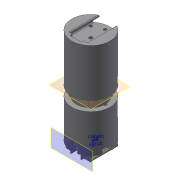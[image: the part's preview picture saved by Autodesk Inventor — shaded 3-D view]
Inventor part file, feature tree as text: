
AUTODESK INVENTOR PART (.ipt)
format: ipt  version: 2018 (Build 220112000, 112)  size: 440,832 bytes
history: native  units: mm
features: sketch x20, extrude x16, fillet x2, plane x2, loft x2, other x2, mirror x1
ambient origin geometry x8: Origin, YZ Plane, XZ Plane, XY Plane, X Axis, Y Axis, Z Axis, Center Point
bodies: Solid1 (feature_tree)
feature tree (45):
  extrude  "base"  Depth=80.0mm TaperAngle=0.0deg
  extrude  "tail_horse_1"  Depth=20.0mm
  mirror  "tail_horse_2"
  fillet  "fillet_tail_horse"  [1 undecoded]
  extrude  "attach_screw"  Depth=20.0mm
  extrude  "attach_screw_head"  Depth=20.0mm TaperAngle=0.0deg
  extrude  "lock_arm"  Depth=30.0mm
  plane  "Work Plane1"
  extrude  "servo_place"  Depth=80.0mm TaperAngle=360.0deg
  sketch  "Sketch7"  dims[d18=0.0mm d19=0.0mm d20=30.0mm]
  sketch  "Sketch8"  dims[d21=6.0mm d22=80.0mm d24=360.0deg]
  sketch  "Sketch9"  dims[d26=20.0mm d27=0.0mm d28=8.0mm]
  extrude  "Extrusion8"  Depth=30.0mm
  extrude  "Extrusion9"  Depth=80.0mm TaperAngle=360.0deg
  sketch  "Sketch12"  dims[d32=10.0mm d33=25.0mm]
  sketch  "Sketch13"  dims[d34=20.0mm d35=65.0mm d36=0.0mm]
  loft  "Loft1"
  loft  "Loft3"
  extrude  "holgura"  Depth=10.0mm
  extrude  "extenson"  Depth=65.0mm TaperAngle=0.0deg
  extrude  "horse_tail_female"  Depth=2.0mm
  extrude  "Extrusion14"  Depth=6.0mm
  fillet  "Fillet2"  Radius=3.0mm
  extrude  "Extrusion15"  TaperAngle=180.0deg  [1 undecoded]
  extrude  "Extrusion17"  Depth=10.0mm
  plane  "Work Plane2"
  extrude  "Extrusion18"  Depth=10.0mm
  extrude  "Extrusion19"  Depth=12.0mm
  sketch  "Sketch1"  dims[d0=80.0mm d1=20.0mm d2=0.0mm]
  sketch  "Sketch2"  dims[d3=15.0mm d4=20.0mm d5=135.0deg]
  sketch  "Sketch3"  dims[d6=15.0mm d7=20.0mm]
  sketch  "Sketch4"  dims[d8=135.0deg d9=20.0mm d10=0.0mm]
  sketch  "Sketch5"  dims[d11=2.0mm d12=30.0mm]
  sketch  "Sketch6"  dims[d13=3.5mm d14=80.0mm d16=360.0deg]
  sketch  "Sketch11"  dims[d29=3.5mm d30=0.0mm d31=0.0mm]
  other  "Edges1"
  other  "Edges4"
  sketch  "Sketch14"  dims[d37=6.0mm d38=2.0mm]
  sketch  "Sketch15"  dims[d39=3.0mm d40=6.0mm d41=3.0mm]
  sketch  "Sketch16"  dims[d42=3.5mm d43=180.0deg]
  sketch  "Sketch17"  dims[d44=1.5mm d46=10.0mm]
  sketch  "Sketch18"  dims[d47=6.0mm d48=10.0mm]
  sketch  "Sketch20"  dims[d49=4.0mm d50=12.0mm]
  sketch  "Sketch21"  dims[d51=11.5mm]
  sketch  "Sketch22"  dims[d52=4.5mm d53=13.0mm d54=9.0mm d55=13.0mm d56=90.0deg d57=8.0mm d58=12.0mm d59=3.0mm d64=10.0mm d65=0.0mm d74=80.0mm d75=8.5mm d76=11.5mm d77=5.5mm d78=11.5mm d79=5.5mm d80=10.0mm d81=0.0mm d82=7.0mm d83=0.0mm d84=90.0deg d85=0.0mm d86=90.0deg d93=0.0mm d94=90.0deg d95=0.0mm d96=90.0deg d97=0.5mm d98=57.0mm d99=21.0mm d100=10.0mm d101=10.0mm d102=0.0mm d103=80.0mm d104=180.0mm d105=0.0mm d106=15.0mm d107=20.0mm d108=135.0deg d109=15.0mm d110=20.0mm d111=135.0deg d112=200.0mm d113=0.0mm d114=8.0mm d115=12.0mm d116=5.0mm d117=12.0mm d118=40.0mm d119=200.0mm d120=0.0mm d121=2.0mm d122=7.0mm d123=200.0mm d124=0.0mm d129=6.0mm d130=6.0mm d131=6.0mm d132=6.0mm d133=6.0mm d134=6.0mm d135=6.0mm d136=20.0mm d137=0.0mm d138=-100.0mm d139=60.0mm d140=80.0mm d143=20.0mm d144=0.0mm d145=6.0mm d146=90.0deg d147=3.0mm d148=20.0mm d149=0.0mm]
note: 2 required parameter values undecoded (feature->parameter linkage not recoverable at this tier; creation-order binding heuristic only, values carry confidence <= 0.55)
